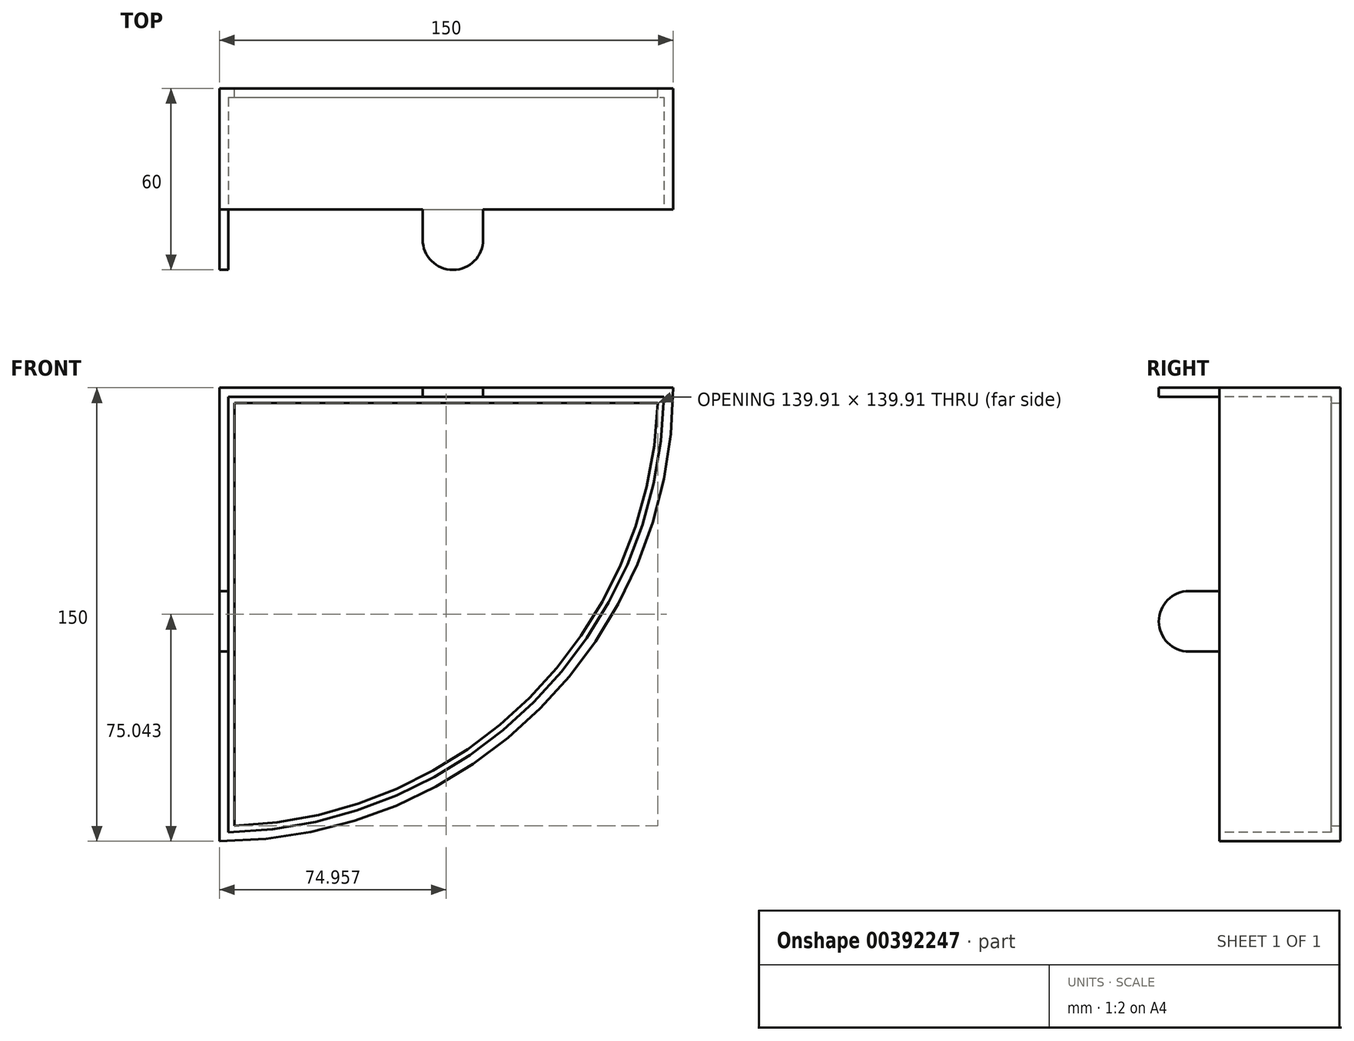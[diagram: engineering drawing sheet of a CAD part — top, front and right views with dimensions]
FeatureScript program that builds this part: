
annotation { "Feature Type Name" : "Feature", "Feature Type Description" : "" }
export const myFeature = defineFeature(function(context is Context, id is Id, definition is map)
    precondition{}
    {
        {
            var Q0;
            Q0=qCreatedBy(makeId("Front.planeOp"),FACE);
            var sketch = newSketch(context, id + "F0", { "sketchPlane" : qUnion([Q0])});
            skArc(sketch, "E0", {"start": v(0, -150) * mm, "mid": v(106.07, -106.07) * mm, "end": v(150, 0) * mm});
            skLineSegment(sketch, "E1", {"start": v(0, 0) * mm, "end": v(150, 0) * mm});
            skLineSegment(sketch, "E2", {"start": v(0, 0) * mm, "end": v(0, -150) * mm});
            skSolve(sketch);
        }
        {
            var Q0;
            Q0 = qSketchRegion(id + "F0", true);
            extrude(context, id + "F1", {"entities" : qUnion([Q0]), "depth" : 40 * mm});
        }
        {
            var Q0;
            Q0=makeQuery(id+"F1.opExtrude","CAP_FACE",FACE,{"disambiguationData":[OSD([sQuery(id+"F0.wireOp",EDGE,"E0"),sQuery(id+"F0.wireOp",EDGE,"E1"),sQuery(id+"F0.wireOp",EDGE,"E2")])],"isStart":false});
            var sketch = newSketch(context, id + "F2", { "sketchPlane" : qUnion([Q0])});
            skLineSegment(sketch, "E3.bottom", {"start": v(3, -67.26) * mm, "end": v(0, -67.26) * mm});
            skLineSegment(sketch, "E3.top", {"start": v(3, -87.26) * mm, "end": v(0, -87.26) * mm});
            skLineSegment(sketch, "E3.left", {"start": v(3, -67.26) * mm, "end": v(3, -87.26) * mm});
            skLineSegment(sketch, "E3.right", {"start": v(0, -67.26) * mm, "end": v(0, -87.26) * mm});
            skLineSegment(sketch, "E4.bottom", {"start": v(67.2, -3) * mm, "end": v(87.21, -3) * mm});
            skLineSegment(sketch, "E4.top", {"start": v(67.2, 0) * mm, "end": v(87.21, 0) * mm});
            skLineSegment(sketch, "E4.left", {"start": v(67.2, -3) * mm, "end": v(67.2, 0) * mm});
            skLineSegment(sketch, "E4.right", {"start": v(87.21, -3) * mm, "end": v(87.21, 0) * mm});
            skSolve(sketch);
        }
        {
            var Q0;
            Q0 = qSketchRegion(id + "F2", true);
            extrude(context, id + "F3", {"entities" : qUnion([Q0]), "operationType" : NewBodyOperationType.ADD, "depth" : 20 * mm});
        }
        {
            var Q0;
            Q0=makeQuery(id+"F3.opExtrude","CAP_EDGE",EDGE,{"disambiguationData":[OSD([sQuery(id+"F2.wireOp",EDGE,"E4.right")])],"isStart":false});
            fillet(context, id + "F4", {"entities" : qUnion([Q0]), "radius" : 10 * mm, "tangentPropagation" : true, "allowEdgeOverflow" : false});
        }
        {
            var Q0;
            Q0=makeQuery(id+"F3.opExtrude","CAP_EDGE",EDGE,{"disambiguationData":[OSD([sQuery(id+"F2.wireOp",EDGE,"E4.left")])],"isStart":false});
            var Q1;
            Q1=makeQuery(id+"F3.opExtrude","CAP_EDGE",EDGE,{"disambiguationData":[OSD([sQuery(id+"F2.wireOp",EDGE,"E3.bottom")])],"isStart":false});
            var Q2;
            Q2=makeQuery(id+"F3.opExtrude","CAP_EDGE",EDGE,{"disambiguationData":[OSD([sQuery(id+"F2.wireOp",EDGE,"E3.top")])],"isStart":false});
            fillet(context, id + "F5", {"entities" : qUnion([Q0, Q1, Q2]), "radius" : 10 * mm, "tangentPropagation" : true, "allowEdgeOverflow" : false});
        }
        {
            var Q0;
            Q0=qCreatedBy(makeId("Front.planeOp"),FACE);
            var sketch = newSketch(context, id + "F6", { "sketchPlane" : qUnion([Q0])});
            skLineSegment(sketch, "E5.0", {"start": v(0, -5) * mm, "end": v(150, -5) * mm});
            skArc(sketch, "E6.0", {"start": v(0, -145) * mm, "mid": v(102.53, -102.53) * mm, "end": v(145, 0) * mm});
            skLineSegment(sketch, "E7.0", {"start": v(5, 0) * mm, "end": v(5, -150) * mm});
            skSolve(sketch);
        }
        {
            var Q0;
            Q0 = qSketchRegion(id + "F6", true);
            extrude(context, id + "F7", {"entities" : qUnion([Q0]), "operationType" : NewBodyOperationType.REMOVE, "endBound" : BoundingType.UP_TO_NEXT, "depth" : 25 * mm});
        }
        {
            var Q0;
            Q0=makeQuery(id+"F1.opExtrude","CAP_FACE",FACE,{"disambiguationData":[OSD([sQuery(id+"F0.wireOp",EDGE,"E0"),sQuery(id+"F0.wireOp",EDGE,"E1"),sQuery(id+"F0.wireOp",EDGE,"E2")])],"isStart":false});
            var sketch = newSketch(context, id + "F8", { "sketchPlane" : qUnion([Q0])});
            skLineSegment(sketch, "E8.0", {"start": v(0, -3) * mm, "end": v(150, -3) * mm});
            skArc(sketch, "E9.0", {"start": v(0, -147) * mm, "mid": v(103.94, -103.94) * mm, "end": v(147, 0) * mm});
            skLineSegment(sketch, "E10.0", {"start": v(3, 0) * mm, "end": v(3, -150) * mm});
            skSolve(sketch);
        }
        {
            var Q0;
            Q0 = qSketchRegion(id + "F8", true);
            extrude(context, id + "F9", {"entities" : qUnion([Q0]), "operationType" : NewBodyOperationType.REMOVE, "oppositeDirection" : true, "depth" : 37 * mm});
        }
    });
